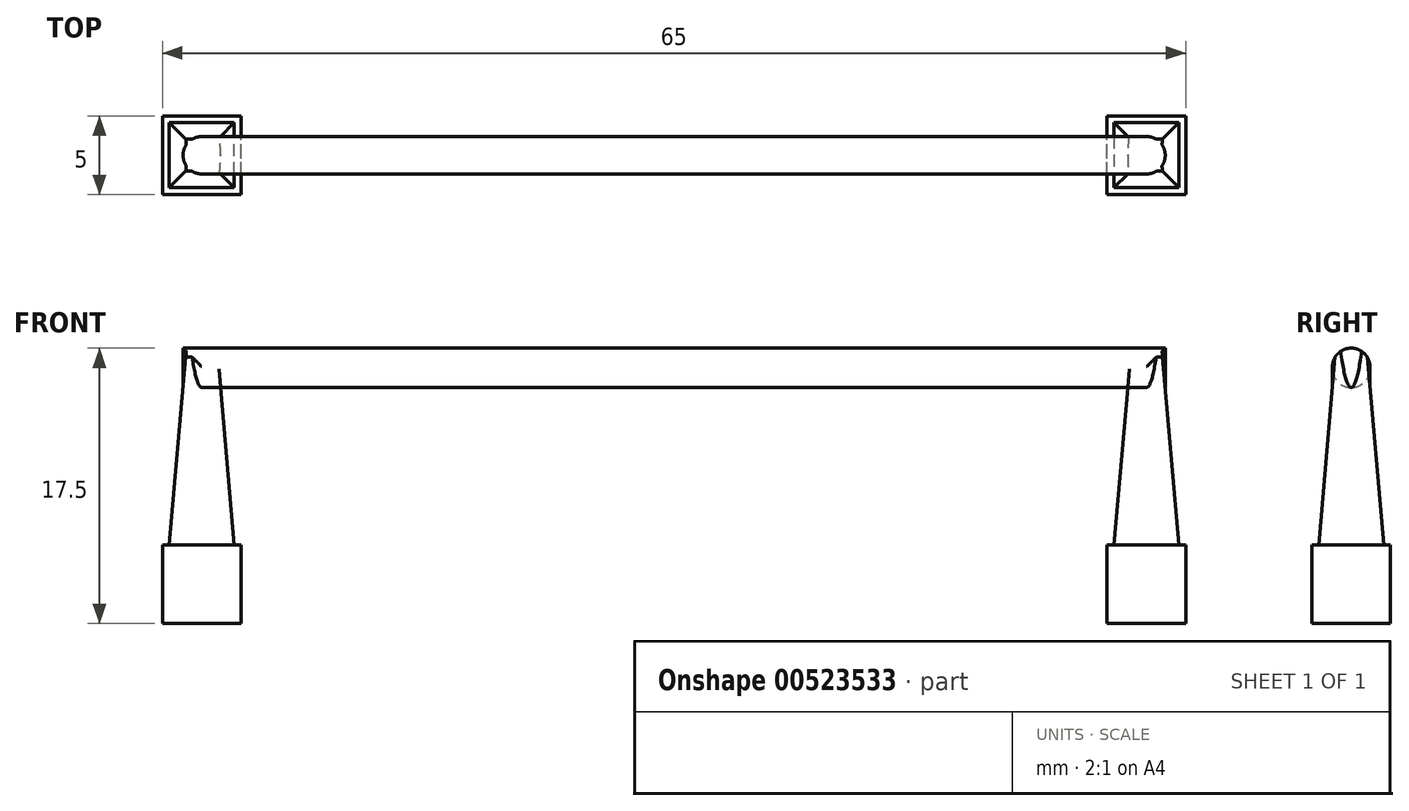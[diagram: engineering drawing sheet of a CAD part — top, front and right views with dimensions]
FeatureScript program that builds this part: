
annotation { "Feature Type Name" : "Feature", "Feature Type Description" : "" }
export const myFeature = defineFeature(function(context is Context, id is Id, definition is map)
    precondition{}
    {
        {
            var Q0;
            Q0=qCreatedBy(makeId("Top.planeOp"),FACE);
            var sketch = newSketch(context, id + "F0", { "sketchPlane" : qUnion([Q0])});
            skLineSegment(sketch, "E0", {"start": v(0, 0) * mm, "end": v(0, 5) * mm});
            skLineSegment(sketch, "E1", {"start": v(0, 5) * mm, "end": v(-5, 5) * mm});
            skLineSegment(sketch, "E2", {"start": v(-5, 5) * mm, "end": v(-5, 0) * mm});
            skLineSegment(sketch, "E3", {"start": v(-5, 0) * mm, "end": v(0, 0) * mm});
            skLineSegment(sketch, "E4", {"start": v(0, 0) * mm, "end": v(55, 0) * mm});
            skLineSegment(sketch, "E5", {"start": v(55, 0) * mm, "end": v(55, 5) * mm});
            skLineSegment(sketch, "E6", {"start": v(55, 5) * mm, "end": v(60, 5) * mm});
            skLineSegment(sketch, "E7", {"start": v(60, 5) * mm, "end": v(60, 0) * mm});
            skLineSegment(sketch, "E8", {"start": v(60, 0) * mm, "end": v(55, 0) * mm});
            skSolve(sketch);
        }
        {
            var Q0;
            Q0=makeQuery(id+"F0.imprint","IMPRINT",FACE,{"disambiguationData":[TD([[makeQuery(id+"F0.imprint","IMPRINT",EDGE,{"derivedFrom":sQuery(id+"F0.wireOp",EDGE,"E0")}),1.0]])]});
            var Q1;
            Q1=makeQuery(id+"F0.imprint","IMPRINT",FACE,{"disambiguationData":[TD([[makeQuery(id+"F0.imprint","IMPRINT",EDGE,{"derivedFrom":sQuery(id+"F0.wireOp",EDGE,"E5")}),-1.0]])]});
            extrude(context, id + "F1", {"entities" : qUnion([Q0, Q1]), "depth" : 5 * mm, "offsetDistance" : 25 * mm});
        }
        {
            var Q0;
            Q0 = qSketchRegion(id + "F0", true);
            extrude(context, id + "F2", {"entities" : qUnion([Q0]), "operationType" : NewBodyOperationType.ADD, "depth" : 15 * mm, "offsetDistance" : 25 * mm, "hasDraft" : true, "draftAngle" : 5 * degree, "draftPullDirection" : true});
        }
        {
            var Q0;
            Q0=makeQuery(id+"F2.opExtrude","CAP_FACE",FACE,{"disambiguationData":[OSD([sQuery(id+"F0.wireOp",EDGE,"E5"),sQuery(id+"F0.wireOp",EDGE,"E6"),sQuery(id+"F0.wireOp",EDGE,"E7"),sQuery(id+"F0.wireOp",EDGE,"E8")])],"isStart":false});
            var sketch = newSketch(context, id + "F3", { "sketchPlane" : qUnion([Q0])});
            skLineSegment(sketch, "E9.0.0", {"start": v(-3.69, 3.69) * mm, "end": v(-3.69, 1.31) * mm});
            skLineSegment(sketch, "E9.0.1", {"start": v(-3.69, 1.31) * mm, "end": v(-1.31, 1.31) * mm});
            skLineSegment(sketch, "E9.0.3", {"start": v(-1.31, 3.69) * mm, "end": v(-3.69, 3.69) * mm});
            skLineSegment(sketch, "E10.0.0", {"start": v(56.31, 1.31) * mm, "end": v(58.69, 1.31) * mm});
            skLineSegment(sketch, "E10.0.1", {"start": v(58.69, 1.31) * mm, "end": v(58.69, 3.69) * mm});
            skLineSegment(sketch, "E10.0.2", {"start": v(58.69, 3.69) * mm, "end": v(56.31, 3.69) * mm});
            skLineSegment(sketch, "E11", {"start": v(-1.31, 3.69) * mm, "end": v(56.31, 3.69) * mm});
            skLineSegment(sketch, "E12", {"start": v(56.31, 1.31) * mm, "end": v(-1.31, 1.31) * mm});
            skSolve(sketch);
        }
        {
            var Q0;
            Q0 = qSketchRegion(id + "F3", true);
            extrude(context, id + "F4", {"entities" : qUnion([Q0]), "operationType" : NewBodyOperationType.ADD, "depth" : 2.5 * mm, "offsetDistance" : 25 * mm});
        }
        {
            var Q0;
            Q0=makeQuery(id+"F4.opExtrude","SWEPT_EDGE",EDGE,{"disambiguationData":[OSD([sQuery(id+"F3.wireOp",EDGE,"E10.0.1"),sQuery(id+"F3.wireOp",EDGE,"E10.0.2")])]});
            var Q1;
            Q1=makeQuery(id+"F4.opExtrude","SWEPT_EDGE",EDGE,{"disambiguationData":[OSD([sQuery(id+"F3.wireOp",EDGE,"E10.0.0"),sQuery(id+"F3.wireOp",EDGE,"E10.0.1")])]});
            var Q2;
            Q2=makeQuery(id+"F4.opExtrude","SWEPT_EDGE",EDGE,{"disambiguationData":[OSD([sQuery(id+"F3.wireOp",EDGE,"E9.0.0"),sQuery(id+"F3.wireOp",EDGE,"E9.0.3")])]});
            var Q3;
            Q3=makeQuery(id+"F4.opExtrude","SWEPT_EDGE",EDGE,{"disambiguationData":[OSD([sQuery(id+"F3.wireOp",EDGE,"E9.0.0"),sQuery(id+"F3.wireOp",EDGE,"E9.0.1")])]});
            fillet(context, id + "F5", {"entities" : qUnion([Q0, Q1, Q2, Q3]), "radius" : 1.18 * mm, "tangentPropagation" : true, "allowEdgeOverflow" : false});
        }
        {
            var Q0;
            Q0=makeQuery(id+"F4.opExtrude","CAP_EDGE",EDGE,{"disambiguationData":[OSD([sQuery(id+"F3.wireOp",EDGE,"E9.0.3"),sQuery(id+"F3.wireOp",EDGE,"E10.0.2"),sQuery(id+"F3.wireOp",EDGE,"E11")])],"isStart":false});
            var Q1;
            Q1=makeQuery(id+"F4.boolean.opBoolean","SPLIT",EDGE,{"derivedFrom":makeQuery(id+"F4.opExtrude","CAP_EDGE",EDGE,{"disambiguationData":[OSD([sQuery(id+"F3.wireOp",EDGE,"E9.0.3"),sQuery(id+"F3.wireOp",EDGE,"E10.0.2"),sQuery(id+"F3.wireOp",EDGE,"E11")])],"isStart":true})});
            var Q2;
            Q2=makeQuery(id+"F4.opExtrude","CAP_EDGE",EDGE,{"disambiguationData":[OSD([sQuery(id+"F3.wireOp",EDGE,"E9.0.1"),sQuery(id+"F3.wireOp",EDGE,"E10.0.0"),sQuery(id+"F3.wireOp",EDGE,"E12")])],"isStart":false});
            var Q3;
            Q3=makeQuery(id+"F4.boolean.opBoolean","SPLIT",EDGE,{"derivedFrom":makeQuery(id+"F4.opExtrude","CAP_EDGE",EDGE,{"disambiguationData":[OSD([sQuery(id+"F3.wireOp",EDGE,"E9.0.1"),sQuery(id+"F3.wireOp",EDGE,"E10.0.0"),sQuery(id+"F3.wireOp",EDGE,"E12")])],"isStart":true})});
            fillet(context, id + "F6", {"entities" : qUnion([Q0, Q1, Q2, Q3]), "radius" : 1.18 * mm, "tangentPropagation" : true, "allowEdgeOverflow" : false});
        }
    });
